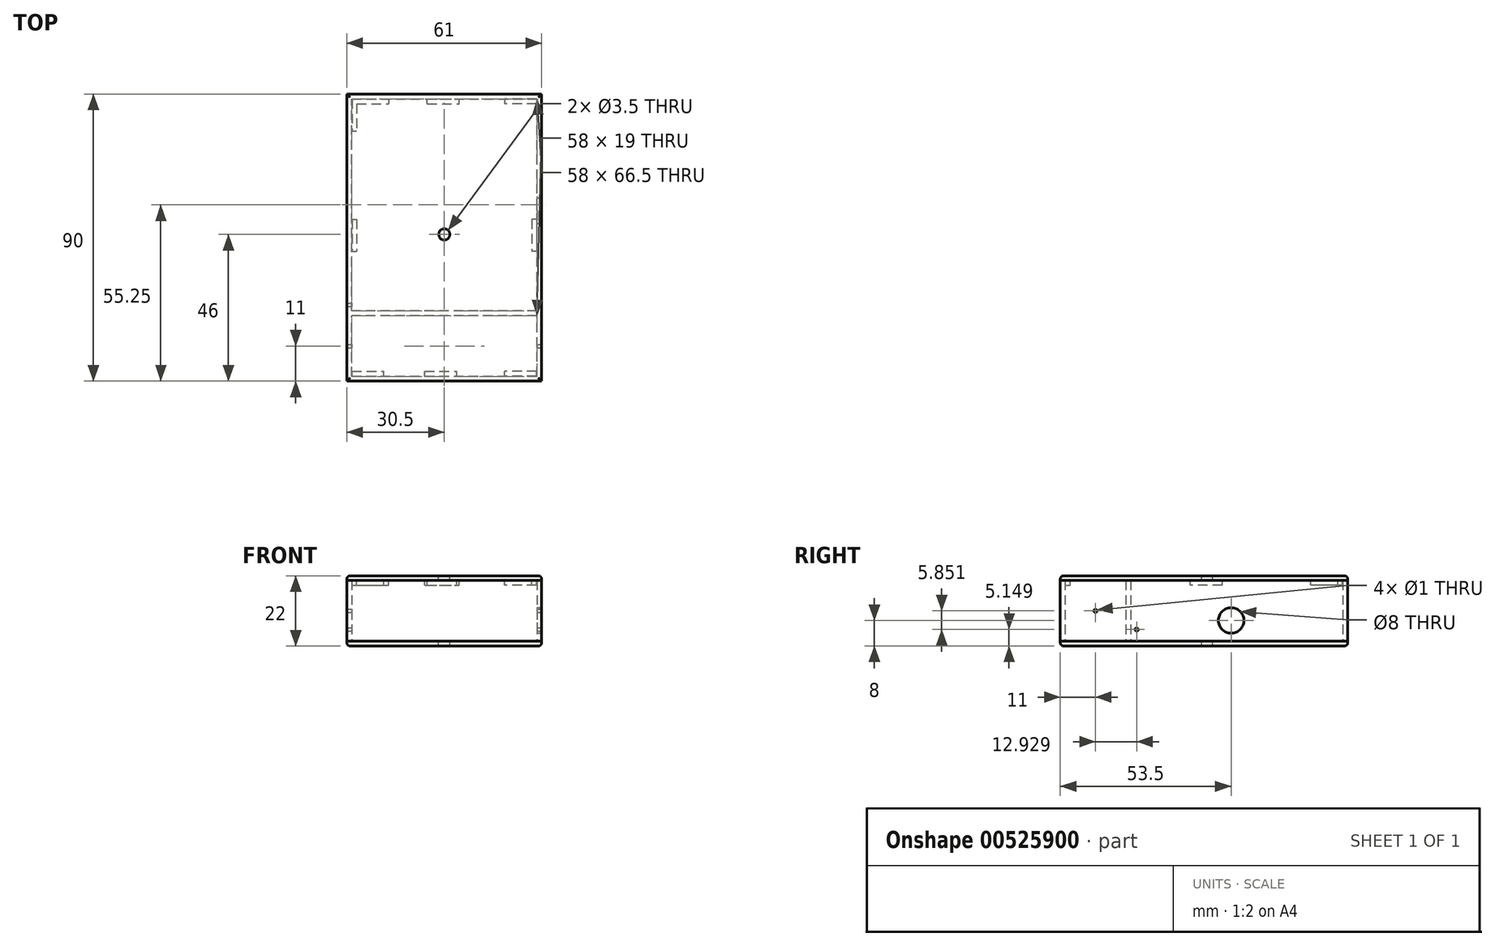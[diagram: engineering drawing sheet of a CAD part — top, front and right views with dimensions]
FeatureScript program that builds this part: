
annotation { "Feature Type Name" : "Feature", "Feature Type Description" : "" }
export const myFeature = defineFeature(function(context is Context, id is Id, definition is map)
    precondition{}
    {
        {
            var Q0;
            Q0=qCreatedBy(makeId("Top.planeOp"),FACE);
            var sketch = newSketch(context, id + "F0", { "sketchPlane" : qUnion([Q0])});
            skLineSegment(sketch, "E0.bottom", {"start": v(29, -9.5) * mm, "end": v(-29, -9.5) * mm});
            skLineSegment(sketch, "E0.top", {"start": v(29, 9.5) * mm, "end": v(-29, 9.5) * mm});
            skLineSegment(sketch, "E0.left", {"start": v(29, -9.5) * mm, "end": v(29, 9.5) * mm});
            skLineSegment(sketch, "E0.right", {"start": v(-29, -9.5) * mm, "end": v(-29, 9.5) * mm});
            skPoint(sketch, "E0.middle", {"position": v(0, 0) * mm});
            skLineSegment(sketch, "E1.0", {"start": v(29, 11) * mm, "end": v(-29, 11) * mm});
            skLineSegment(sketch, "E1.2", {"start": v(30.5, -11) * mm, "end": v(-30.5, -11) * mm});
            skLineSegment(sketch, "E2.bottom", {"start": v(-29, 11) * mm, "end": v(29, 11) * mm});
            skLineSegment(sketch, "E2.top", {"start": v(-30.5, 79) * mm, "end": v(30.5, 79) * mm});
            skLineSegment(sketch, "E2.right", {"start": v(30.5, -11) * mm, "end": v(30.5, 79) * mm});
            skLineSegment(sketch, "E3.1", {"start": v(-29, 77.5) * mm, "end": v(29, 77.5) * mm});
            skLineSegment(sketch, "E4.trimOffspring", {"start": v(-30.5, -11) * mm, "end": v(-30.5, 79) * mm});
            skLineSegment(sketch, "E5.trimOffspring", {"start": v(-29, 11) * mm, "end": v(-29, 77.5) * mm});
            skLineSegment(sketch, "E6.trimOffspring", {"start": v(29, 11) * mm, "end": v(29, 77.5) * mm});
            skSolve(sketch);
        }
        {
            var Q0;
            Q0 = qSketchRegion(id + "F0", true);
            extrude(context, id + "F1", {"entities" : qUnion([Q0]), "depth" : 19 * mm, "offsetDistance" : 25 * mm});
        }
        {
            var Q0;
            Q0=makeQuery(id+"F1.opExtrude","SWEPT_FACE",FACE,{"disambiguationData":[OSD([sQuery(id+"F0.wireOp",EDGE,"E2.right")])]});
            var sketch = newSketch(context, id + "F2", { "sketchPlane" : qUnion([Q0])});
            skCircle(sketch, "E7", {"center": v(0, 9.5) * mm, "radius": 0.5 * mm});
            skPoint(sketch, "E7.centerSnap0", {"position": v(-11, 9.5) * mm});
            skSolve(sketch);
        }
        {
            var Q0;
            Q0=makeQuery(id+"F2.imprint","IMPRINT",FACE,{"disambiguationData":[TD([[makeQuery(id+"F2.imprint","IMPRINT",EDGE,{"derivedFrom":sQuery(id+"F2.wireOp",EDGE,"E7")}),1.0]])]});
            var Q1;
            Q1=sQuery(id+"F2.wireOp",EDGE,"E7");
            extrude(context, id + "F3", {"entities" : qUnion([Q0]), "operationType" : NewBodyOperationType.REMOVE, "surfaceEntities" : qUnion([Q1]), "endBound" : BoundingType.THROUGH_ALL, "oppositeDirection" : true, "depth" : 25 * mm, "offsetDistance" : 25 * mm});
        }
        {
            var Q0;
            Q0=makeQuery(id+"F1.opExtrude","SWEPT_FACE",FACE,{"disambiguationData":[OSD([sQuery(id+"F0.wireOp",EDGE,"E6.trimOffspring")])]});
            var sketch = newSketch(context, id + "F4", { "sketchPlane" : qUnion([Q0])});
            skCircle(sketch, "E8", {"center": v(-12.93, 3.65) * mm, "radius": 0.5 * mm});
            skSolve(sketch);
        }
        {
            var Q0;
            Q0=makeQuery(id+"F4.imprint","IMPRINT",FACE,{"disambiguationData":[TD([[makeQuery(id+"F4.imprint","IMPRINT",EDGE,{"derivedFrom":sQuery(id+"F4.wireOp",EDGE,"E8")}),1.0]])]});
            extrude(context, id + "F5", {"entities" : qUnion([Q0]), "operationType" : NewBodyOperationType.REMOVE, "endBound" : BoundingType.SYMMETRIC, "depth" : 120 * mm, "offsetDistance" : 25 * mm});
        }
        {
            var Q0;
            Q0=makeQuery(id+"F1.opExtrude","CAP_FACE",FACE,{"disambiguationData":[OSD([sQuery(id+"F0.wireOp",EDGE,"E0.bottom"),sQuery(id+"F0.wireOp",EDGE,"E0.top"),sQuery(id+"F0.wireOp",EDGE,"E0.left"),sQuery(id+"F0.wireOp",EDGE,"E0.right"),sQuery(id+"F0.wireOp",EDGE,"E1.2"),sQuery(id+"F0.wireOp",EDGE,"E2.bottom"),sQuery(id+"F0.wireOp",EDGE,"E2.top"),sQuery(id+"F0.wireOp",EDGE,"E2.right"),sQuery(id+"F0.wireOp",EDGE,"E3.1"),sQuery(id+"F0.wireOp",EDGE,"E4.trimOffspring"),sQuery(id+"F0.wireOp",EDGE,"E5.trimOffspring"),sQuery(id+"F0.wireOp",EDGE,"E6.trimOffspring")])],"isStart":false});
            var sketch = newSketch(context, id + "F6", { "sketchPlane" : qUnion([Q0])});
            skLineSegment(sketch, "E9.bottom", {"start": v(-30.5, 79) * mm, "end": v(30.5, 79) * mm});
            skLineSegment(sketch, "E9.top", {"start": v(-30.5, -11) * mm, "end": v(30.5, -11) * mm});
            skLineSegment(sketch, "E9.left", {"start": v(-30.5, 79) * mm, "end": v(-30.5, -11) * mm});
            skLineSegment(sketch, "E9.right", {"start": v(30.5, 79) * mm, "end": v(30.5, -11) * mm});
            skSolve(sketch);
        }
        {
            var Q0;
            Q0 = qSketchRegion(id + "F6", true);
            extrude(context, id + "F7", {"entities" : qUnion([Q0]), "depth" : 1.5 * mm, "offsetDistance" : 25 * mm});
        }
        {
            var Q0;
            Q0=makeQuery(id+"F7.opExtrude","SWEPT_BODY",BODY,{"disambiguationData":[OSD([sQuery(id+"F6.wireOp",EDGE,"E9.bottom"),sQuery(id+"F6.wireOp",EDGE,"E9.top"),sQuery(id+"F6.wireOp",EDGE,"E9.left"),sQuery(id+"F6.wireOp",EDGE,"E9.right")])]});
            transform(context, id + "F8", {"entities" : qUnion([Q0]), "transformType" : TransformType.TRANSLATION_3D, "dx" : 0 * mm, "dy" : 0 * mm, "dz" : -19 * mm, "makeCopy" : true});
        }
        {
            var Q0;
            Q0=makeQuery(id+"F8.opPattern","COPY",EDGE,{"derivedFrom":makeQuery(id+"F7.opExtrude","CAP_EDGE",EDGE,{"disambiguationData":[OSD([sQuery(id+"F6.wireOp",EDGE,"E9.bottom")])],"isStart":true}),"instanceName":"1"});
            var Q1;
            Q1=makeQuery(id+"F8.opPattern","COPY",EDGE,{"derivedFrom":makeQuery(id+"F7.opExtrude","CAP_EDGE",EDGE,{"disambiguationData":[OSD([sQuery(id+"F6.wireOp",EDGE,"E9.right")])],"isStart":true}),"instanceName":"1"});
            var Q2;
            Q2=makeQuery(id+"F8.opPattern","COPY",EDGE,{"derivedFrom":makeQuery(id+"F7.opExtrude","CAP_EDGE",EDGE,{"disambiguationData":[OSD([sQuery(id+"F6.wireOp",EDGE,"E9.left")])],"isStart":true}),"instanceName":"1"});
            var Q3;
            Q3=makeQuery(id+"F8.opPattern","COPY",EDGE,{"derivedFrom":makeQuery(id+"F7.opExtrude","CAP_EDGE",EDGE,{"disambiguationData":[OSD([sQuery(id+"F6.wireOp",EDGE,"E9.top")])],"isStart":true}),"instanceName":"1"});
            fillet(context, id + "F9", {"entities" : qUnion([Q0, Q1, Q2, Q3]), "radius" : 1 * mm, "tangentPropagation" : true, "allowEdgeOverflow" : false});
        }
        {
            var Q0;
            Q0=makeQuery(id+"F8.opPattern","COPY",BODY,{"derivedFrom":makeQuery(id+"F7.opExtrude","SWEPT_BODY",BODY,{"disambiguationData":[OSD([sQuery(id+"F6.wireOp",EDGE,"E9.bottom"),sQuery(id+"F6.wireOp",EDGE,"E9.top"),sQuery(id+"F6.wireOp",EDGE,"E9.left"),sQuery(id+"F6.wireOp",EDGE,"E9.right")])]}),"instanceName":"1"});
            var Q1;
            Q1=qCreatedBy(makeId("Top.planeOp"),FACE);
            transform(context, id + "F10", {"entities" : qUnion([Q0]), "transformType" : TransformType.TRANSLATION_DISTANCE, "transformDirection" : qUnion([Q1]), "distance" : 1.5 * mm, "oppositeDirection" : true, "makeCopy" : false});
        }
        {
            var Q0;
            Q0=makeQuery(id+"F7.opExtrude","CAP_EDGE",EDGE,{"disambiguationData":[OSD([sQuery(id+"F6.wireOp",EDGE,"E9.bottom")])],"isStart":false});
            var Q1;
            Q1=makeQuery(id+"F7.opExtrude","CAP_EDGE",EDGE,{"disambiguationData":[OSD([sQuery(id+"F6.wireOp",EDGE,"E9.left")])],"isStart":false});
            var Q2;
            Q2=makeQuery(id+"F7.opExtrude","CAP_EDGE",EDGE,{"disambiguationData":[OSD([sQuery(id+"F6.wireOp",EDGE,"E9.right")])],"isStart":false});
            var Q3;
            Q3=makeQuery(id+"F7.opExtrude","CAP_EDGE",EDGE,{"disambiguationData":[OSD([sQuery(id+"F6.wireOp",EDGE,"E9.top")])],"isStart":false});
            fillet(context, id + "F11", {"entities" : qUnion([Q0, Q1, Q2, Q3]), "radius" : 1 * mm, "tangentPropagation" : true, "allowEdgeOverflow" : false});
        }
        {
            var Q0;
            Q0=makeQuery(id+"F7.opExtrude","CAP_FACE",FACE,{"disambiguationData":[OSD([sQuery(id+"F6.wireOp",EDGE,"E9.bottom"),sQuery(id+"F6.wireOp",EDGE,"E9.top"),sQuery(id+"F6.wireOp",EDGE,"E9.left"),sQuery(id+"F6.wireOp",EDGE,"E9.right")])],"isStart":false});
            var sketch = newSketch(context, id + "F12", { "sketchPlane" : qUnion([Q0])});
            skCircle(sketch, "E10", {"center": v(0, 35) * mm, "radius": 1.75 * mm});
            skSolve(sketch);
        }
        {
            var Q0;
            Q0=makeQuery(id+"F12.imprint","IMPRINT",FACE,{"disambiguationData":[TD([[makeQuery(id+"F12.imprint","IMPRINT",EDGE,{"derivedFrom":sQuery(id+"F12.wireOp",EDGE,"E10")}),1.0]])]});
            var Q1;
            Q1=sQuery(id+"F12.wireOp",EDGE,"E10");
            extrude(context, id + "F13", {"entities" : qUnion([Q0]), "operationType" : NewBodyOperationType.REMOVE, "surfaceEntities" : qUnion([Q1]), "endBound" : BoundingType.THROUGH_ALL, "oppositeDirection" : true, "depth" : 25 * mm, "offsetDistance" : 25 * mm});
        }
        {
            var Q0;
            Q0=makeQuery(id+"F1.opExtrude","SWEPT_FACE",FACE,{"disambiguationData":[OSD([sQuery(id+"F0.wireOp",EDGE,"E2.right")])]});
            var sketch = newSketch(context, id + "F14", { "sketchPlane" : qUnion([Q0])});
            skCircle(sketch, "E11", {"center": v(42.5, 6.5) * mm, "radius": 4 * mm});
            skSolve(sketch);
        }
        {
            var Q0;
            Q0=makeQuery(id+"F14.imprint","IMPRINT",FACE,{"disambiguationData":[TD([[makeQuery(id+"F14.imprint","IMPRINT",EDGE,{"derivedFrom":sQuery(id+"F14.wireOp",EDGE,"E11")}),1.0]])]});
            extrude(context, id + "F15", {"entities" : qUnion([Q0]), "operationType" : NewBodyOperationType.REMOVE, "endBound" : BoundingType.UP_TO_NEXT, "oppositeDirection" : true, "depth" : 25 * mm, "offsetDistance" : 25 * mm});
        }
        {
            var Q0;
            Q0=makeQuery(id+"F7.opExtrude","CAP_FACE",FACE,{"disambiguationData":[OSD([sQuery(id+"F6.wireOp",EDGE,"E9.bottom"),sQuery(id+"F6.wireOp",EDGE,"E9.top"),sQuery(id+"F6.wireOp",EDGE,"E9.left"),sQuery(id+"F6.wireOp",EDGE,"E9.right")])],"isStart":true});
            var sketch = newSketch(context, id + "F16", { "sketchPlane" : qUnion([Q0])});
            skLineSegment(sketch, "E12.bottom", {"start": v(-28.9, 9.4) * mm, "end": v(-18.9, 9.4) * mm});
            skLineSegment(sketch, "E12.top", {"start": v(-28.9, 7.9) * mm, "end": v(-18.9, 7.9) * mm});
            skLineSegment(sketch, "E12.left", {"start": v(-28.9, 9.4) * mm, "end": v(-28.9, 7.9) * mm});
            skLineSegment(sketch, "E12.right", {"start": v(-18.9, 9.4) * mm, "end": v(-18.9, 7.9) * mm});
            skLineSegment(sketch, "E13.bottom", {"start": v(0.67, 10.25) * mm, "end": v(0.44, 10.25) * mm});
            skLineSegment(sketch, "E13.top", {"start": v(0.67, 10.25) * mm, "end": v(0.44, 10.25) * mm});
            skLineSegment(sketch, "E13.left", {"start": v(0.67, 10.25) * mm, "end": v(0.67, 10.25) * mm});
            skLineSegment(sketch, "E13.right", {"start": v(0.44, 10.25) * mm, "end": v(0.44, 10.25) * mm});
            skLineSegment(sketch, "E14.bottom", {"start": v(-28.9, 7.9) * mm, "end": v(-27.4, 7.9) * mm});
            skLineSegment(sketch, "E14.top", {"start": v(-28.9, -2.1) * mm, "end": v(-27.4, -2.1) * mm});
            skLineSegment(sketch, "E14.left", {"start": v(-28.9, 7.9) * mm, "end": v(-28.9, -2.1) * mm});
            skLineSegment(sketch, "E14.right", {"start": v(-27.4, 7.9) * mm, "end": v(-27.4, -2.1) * mm});
            skLineSegment(sketch, "E15.bottom", {"start": v(28.9, 9.4) * mm, "end": v(18.9, 9.4) * mm});
            skLineSegment(sketch, "E15.top", {"start": v(28.9, 7.9) * mm, "end": v(18.9, 7.9) * mm});
            skLineSegment(sketch, "E15.left", {"start": v(28.9, 9.4) * mm, "end": v(28.9, 7.9) * mm});
            skLineSegment(sketch, "E15.right", {"start": v(18.9, 9.4) * mm, "end": v(18.9, 7.9) * mm});
            skLineSegment(sketch, "E16.bottom", {"start": v(28.9, 7.9) * mm, "end": v(27.4, 7.9) * mm});
            skLineSegment(sketch, "E16.top", {"start": v(28.9, -2.1) * mm, "end": v(27.4, -2.1) * mm});
            skLineSegment(sketch, "E16.left", {"start": v(28.9, 7.9) * mm, "end": v(28.9, -2.1) * mm});
            skLineSegment(sketch, "E16.right", {"start": v(27.4, 7.9) * mm, "end": v(27.4, -2.1) * mm});
            skLineSegment(sketch, "E17.bottom", {"start": v(-28.9, -39.7) * mm, "end": v(-27.4, -39.7) * mm});
            skLineSegment(sketch, "E17.top", {"start": v(-28.9, -29.7) * mm, "end": v(-27.4, -29.7) * mm});
            skLineSegment(sketch, "E17.left", {"start": v(-28.9, -39.7) * mm, "end": v(-28.9, -29.7) * mm});
            skLineSegment(sketch, "E17.right", {"start": v(-27.4, -39.7) * mm, "end": v(-27.4, -29.7) * mm});
            skLineSegment(sketch, "E18.bottom", {"start": v(28.9, -39.7) * mm, "end": v(27.4, -39.7) * mm});
            skLineSegment(sketch, "E18.top", {"start": v(28.9, -29.7) * mm, "end": v(27.4, -29.7) * mm});
            skLineSegment(sketch, "E18.left", {"start": v(28.9, -39.7) * mm, "end": v(28.9, -29.7) * mm});
            skLineSegment(sketch, "E18.right", {"start": v(27.4, -39.7) * mm, "end": v(27.4, -29.7) * mm});
            skLineSegment(sketch, "E19.bottom", {"start": v(-28.9, -77.4) * mm, "end": v(-27.4, -77.4) * mm});
            skLineSegment(sketch, "E19.top", {"start": v(-28.9, -67.4) * mm, "end": v(-27.4, -67.4) * mm});
            skLineSegment(sketch, "E19.left", {"start": v(-28.9, -77.4) * mm, "end": v(-28.9, -67.4) * mm});
            skLineSegment(sketch, "E19.right", {"start": v(-27.4, -77.4) * mm, "end": v(-27.4, -67.4) * mm});
            skLineSegment(sketch, "E20.bottom", {"start": v(-27.4, -77.4) * mm, "end": v(-17.4, -77.4) * mm});
            skLineSegment(sketch, "E20.top", {"start": v(-27.4, -75.9) * mm, "end": v(-17.4, -75.9) * mm});
            skLineSegment(sketch, "E20.left", {"start": v(-27.4, -77.4) * mm, "end": v(-27.4, -75.9) * mm});
            skLineSegment(sketch, "E20.right", {"start": v(-17.4, -77.4) * mm, "end": v(-17.4, -75.9) * mm});
            skLineSegment(sketch, "E21.bottom", {"start": v(28.9, -77.4) * mm, "end": v(18.9, -77.4) * mm});
            skLineSegment(sketch, "E21.top", {"start": v(28.9, -75.9) * mm, "end": v(18.9, -75.9) * mm});
            skLineSegment(sketch, "E21.left", {"start": v(28.9, -77.4) * mm, "end": v(28.9, -75.9) * mm});
            skLineSegment(sketch, "E21.right", {"start": v(18.9, -77.4) * mm, "end": v(18.9, -75.9) * mm});
            skLineSegment(sketch, "E22.bottom", {"start": v(28.9, -75.9) * mm, "end": v(27.4, -75.9) * mm});
            skLineSegment(sketch, "E22.top", {"start": v(28.9, -65.9) * mm, "end": v(27.4, -65.9) * mm});
            skLineSegment(sketch, "E22.left", {"start": v(28.9, -75.9) * mm, "end": v(28.9, -65.9) * mm});
            skLineSegment(sketch, "E22.right", {"start": v(27.4, -75.9) * mm, "end": v(27.4, -65.9) * mm});
            skPoint(sketch, "E23.oppositeSnap0", {"position": v(-23.9, 7.9) * mm});
            skLineSegment(sketch, "E23.bottom", {"start": v(-6.08, 9.4) * mm, "end": v(3.92, 9.4) * mm});
            skLineSegment(sketch, "E23.top", {"start": v(-6.08, 7.9) * mm, "end": v(3.92, 7.9) * mm});
            skLineSegment(sketch, "E23.left", {"start": v(-6.08, 9.4) * mm, "end": v(-6.08, 7.9) * mm});
            skLineSegment(sketch, "E23.right", {"start": v(3.92, 9.4) * mm, "end": v(3.92, 7.9) * mm});
            skLineSegment(sketch, "E24.bottom", {"start": v(-5.31, -77.4) * mm, "end": v(4.69, -77.4) * mm});
            skLineSegment(sketch, "E24.top", {"start": v(-5.31, -75.9) * mm, "end": v(4.69, -75.9) * mm});
            skLineSegment(sketch, "E24.left", {"start": v(-5.31, -75.9) * mm, "end": v(-5.31, -77.4) * mm});
            skLineSegment(sketch, "E24.right", {"start": v(4.69, -75.9) * mm, "end": v(4.69, -77.4) * mm});
            skSolve(sketch);
        }
        {
            var Q0;
            Q0=makeQuery(id+"F16.imprint","IMPRINT",FACE,{"disambiguationData":[TD([[makeQuery(id+"F16.imprint","IMPRINT",EDGE,{"derivedFrom":sQuery(id+"F16.wireOp",EDGE,"E12.bottom")}),-1.0]])]});
            var Q1;
            Q1=makeQuery(id+"F16.imprint","IMPRINT",FACE,{"disambiguationData":[TD([[makeQuery(id+"F16.imprint","IMPRINT",EDGE,{"derivedFrom":sQuery(id+"F16.wireOp",EDGE,"E14.bottom")}),-1.0]])]});
            var Q2;
            Q2=makeQuery(id+"F16.imprint","IMPRINT",FACE,{"disambiguationData":[TD([[makeQuery(id+"F16.imprint","IMPRINT",EDGE,{"derivedFrom":sQuery(id+"F16.wireOp",EDGE,"E17.bottom")}),1.0]])]});
            var Q3;
            Q3=makeQuery(id+"F16.imprint","IMPRINT",FACE,{"disambiguationData":[TD([[makeQuery(id+"F16.imprint","IMPRINT",EDGE,{"derivedFrom":sQuery(id+"F16.wireOp",EDGE,"E15.bottom")}),1.0]])]});
            var Q4;
            Q4=makeQuery(id+"F16.imprint","IMPRINT",FACE,{"disambiguationData":[TD([[makeQuery(id+"F16.imprint","IMPRINT",EDGE,{"derivedFrom":sQuery(id+"F16.wireOp",EDGE,"E16.bottom")}),1.0]])]});
            var Q5;
            Q5=makeQuery(id+"F16.imprint","IMPRINT",FACE,{"disambiguationData":[TD([[makeQuery(id+"F16.imprint","IMPRINT",EDGE,{"derivedFrom":sQuery(id+"F16.wireOp",EDGE,"E18.bottom")}),-1.0]])]});
            var Q6;
            Q6=makeQuery(id+"F16.imprint","IMPRINT",FACE,{"disambiguationData":[TD([[makeQuery(id+"F16.imprint","IMPRINT",EDGE,{"derivedFrom":sQuery(id+"F16.wireOp",EDGE,"E22.bottom")}),-1.0]])]});
            var Q7;
            Q7=makeQuery(id+"F16.imprint","IMPRINT",FACE,{"disambiguationData":[TD([[makeQuery(id+"F16.imprint","IMPRINT",EDGE,{"derivedFrom":sQuery(id+"F16.wireOp",EDGE,"E21.bottom")}),-1.0]])]});
            var Q8;
            Q8=makeQuery(id+"F16.imprint","IMPRINT",FACE,{"disambiguationData":[TD([[makeQuery(id+"F16.imprint","IMPRINT",EDGE,{"derivedFrom":sQuery(id+"F16.wireOp",EDGE,"E20.bottom")}),1.0]])]});
            var Q9;
            Q9=makeQuery(id+"F16.imprint","IMPRINT",FACE,{"disambiguationData":[TD([[makeQuery(id+"F16.imprint","IMPRINT",EDGE,{"derivedFrom":sQuery(id+"F16.wireOp",EDGE,"E19.bottom")}),1.0]])]});
            var Q10;
            Q10=makeQuery(id+"F16.imprint","IMPRINT",FACE,{"disambiguationData":[TD([[makeQuery(id+"F16.imprint","IMPRINT",EDGE,{"derivedFrom":sQuery(id+"F16.wireOp",EDGE,"E23.bottom")}),-1.0]])]});
            var Q11;
            Q11=makeQuery(id+"F16.imprint","IMPRINT",FACE,{"disambiguationData":[TD([[makeQuery(id+"F16.imprint","IMPRINT",EDGE,{"derivedFrom":sQuery(id+"F16.wireOp",EDGE,"E24.bottom")}),1.0]])]});
            extrude(context, id + "F17", {"entities" : qUnion([Q0, Q1, Q2, Q3, Q4, Q5, Q6, Q7, Q8, Q9, Q10, Q11]), "operationType" : NewBodyOperationType.ADD, "depth" : 1.5 * mm, "offsetDistance" : 25 * mm});
        }
    });
